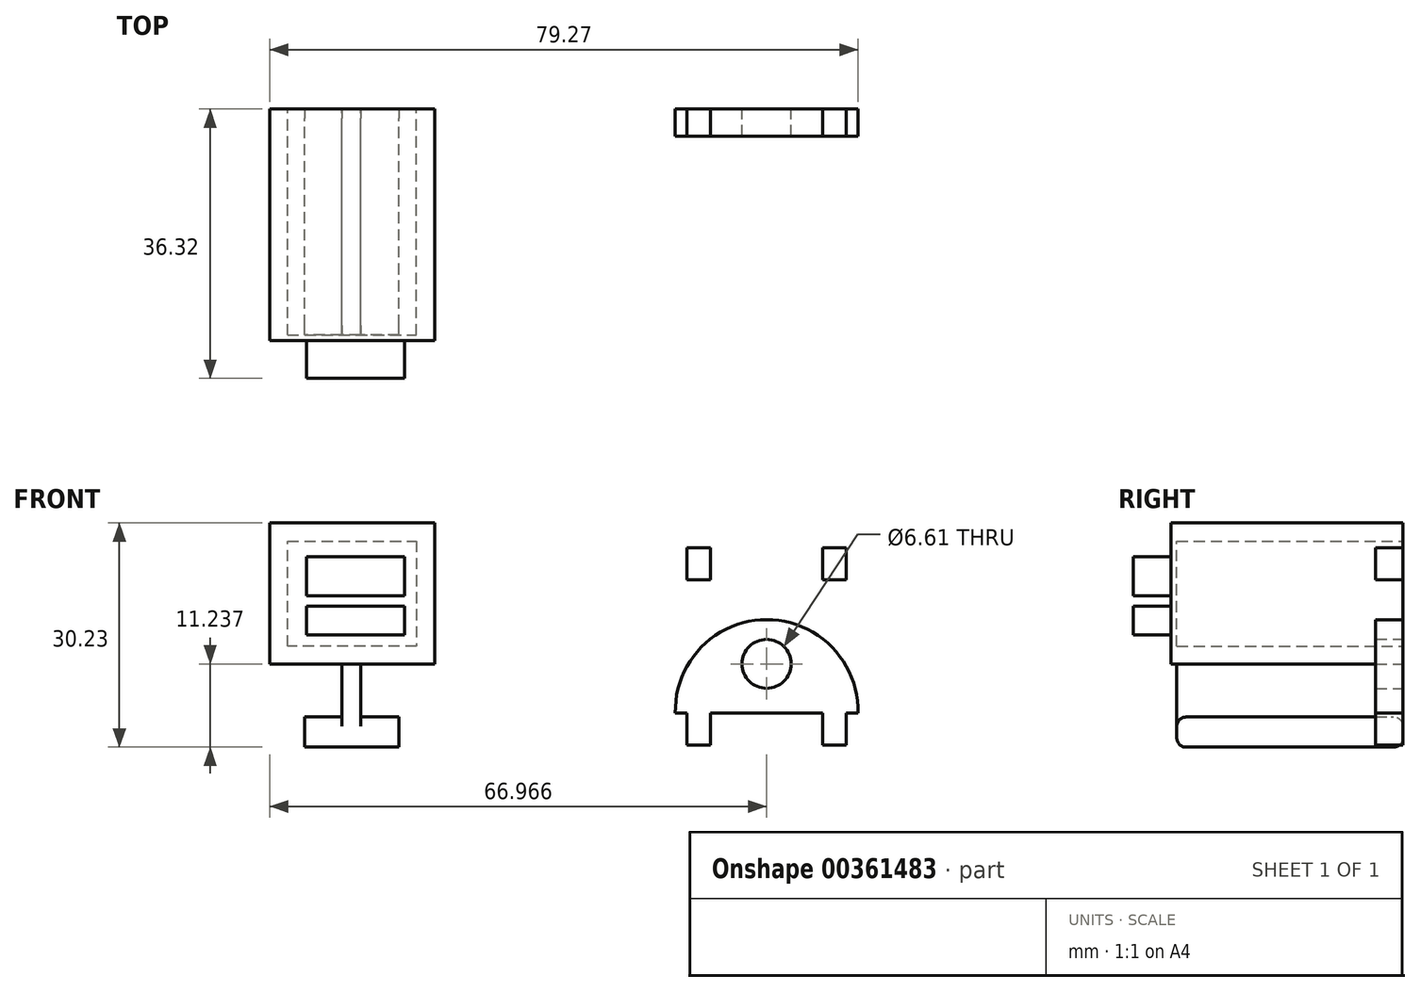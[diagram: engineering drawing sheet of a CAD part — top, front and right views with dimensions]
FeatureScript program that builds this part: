
annotation { "Feature Type Name" : "Feature", "Feature Type Description" : "" }
export const myFeature = defineFeature(function(context is Context, id is Id, definition is map)
    precondition{}
    {
        {
            var Q0;
            Q0=qCreatedBy(makeId("Front.planeOp"),FACE);
            var sketch = newSketch(context, id + "F0", { "sketchPlane" : qUnion([Q0])});
            skLineSegment(sketch, "E0", {"start": v(-32.35, 35.97) * mm, "end": v(-10.13, 35.97) * mm});
            skLineSegment(sketch, "E1", {"start": v(-10.13, 35.97) * mm, "end": v(-10.13, 16.92) * mm});
            skLineSegment(sketch, "E2", {"start": v(-10.13, 16.92) * mm, "end": v(-32.35, 16.92) * mm});
            skLineSegment(sketch, "E3", {"start": v(-32.35, 16.92) * mm, "end": v(-32.35, 35.97) * mm});
            skLineSegment(sketch, "E4", {"start": v(-22.6, 16.92) * mm, "end": v(-22.6, 9.8) * mm});
            skLineSegment(sketch, "E5", {"start": v(-20.06, 16.92) * mm, "end": v(-20.06, 9.8) * mm});
            skLineSegment(sketch, "E6", {"start": v(-22.6, 9.8) * mm, "end": v(-27.6, 9.8) * mm});
            skLineSegment(sketch, "E7", {"start": v(-22.6, 16.92) * mm, "end": v(-20.06, 16.92) * mm});
            skLineSegment(sketch, "E8", {"start": v(-27.6, 9.8) * mm, "end": v(-27.6, 5.74) * mm});
            skLineSegment(sketch, "E9", {"start": v(-27.6, 5.74) * mm, "end": v(-14.9, 5.74) * mm});
            skLineSegment(sketch, "E10", {"start": v(-14.9, 5.74) * mm, "end": v(-14.9, 9.8) * mm});
            skLineSegment(sketch, "E11", {"start": v(-14.9, 9.8) * mm, "end": v(-20.06, 9.8) * mm});
            skLineSegment(sketch, "E12.0", {"start": v(-29.94, 33.55) * mm, "end": v(-12.55, 33.55) * mm});
            skLineSegment(sketch, "E12.1", {"start": v(-29.94, 19.33) * mm, "end": v(-29.94, 33.55) * mm});
            skLineSegment(sketch, "E12.2", {"start": v(-12.55, 19.33) * mm, "end": v(-29.94, 19.33) * mm});
            skLineSegment(sketch, "E12.3", {"start": v(-12.55, 33.55) * mm, "end": v(-12.55, 19.33) * mm});
            skLineSegment(sketch, "E13", {"start": v(-21.33, 16.92) * mm, "end": v(-21.25, 5.74) * mm});
            skSolve(sketch);
        }
        {
            var Q0;
            Q0 = qSketchRegion(id + "F0", true);
            extrude(context, id + "F1", {"entities" : qUnion([Q0]), "depth" : 30.48 * mm});
        }
        {
            var Q0;
            Q0=makeQuery(id+"F1.opExtrude","CAP_FACE",FACE,{"disambiguationData":[OSD([sQuery(id+"F0.wireOp",EDGE,"E0"),sQuery(id+"F0.wireOp",EDGE,"E1"),sQuery(id+"F0.wireOp",EDGE,"E2"),sQuery(id+"F0.wireOp",EDGE,"E3"),sQuery(id+"F0.wireOp",EDGE,"E4"),sQuery(id+"F0.wireOp",EDGE,"E5"),sQuery(id+"F0.wireOp",EDGE,"E6"),sQuery(id+"F0.wireOp",EDGE,"E8"),sQuery(id+"F0.wireOp",EDGE,"E9"),sQuery(id+"F0.wireOp",EDGE,"E10"),sQuery(id+"F0.wireOp",EDGE,"E11"),sQuery(id+"F0.wireOp",EDGE,"E12.0"),sQuery(id+"F0.wireOp",EDGE,"E12.1"),sQuery(id+"F0.wireOp",EDGE,"E12.2"),sQuery(id+"F0.wireOp",EDGE,"E12.3")])],"isStart":false});
            var sketch = newSketch(context, id + "F2", { "sketchPlane" : qUnion([Q0])});
            skLineSegment(sketch, "E14", {"start": v(-32.35, 16.92) * mm, "end": v(-10.13, 16.92) * mm});
            skLineSegment(sketch, "E15", {"start": v(-10.13, 16.92) * mm, "end": v(-10.13, 35.97) * mm});
            skLineSegment(sketch, "E16", {"start": v(-10.13, 35.97) * mm, "end": v(-32.35, 35.97) * mm});
            skLineSegment(sketch, "E17", {"start": v(-32.35, 35.97) * mm, "end": v(-32.35, 16.92) * mm});
            skSolve(sketch);
        }
        {
            var Q0;
            Q0=makeQuery(id+"F2.imprint","IMPRINT",FACE,{"disambiguationData":[TD([[makeQuery(id+"F2.imprint","IMPRINT",EDGE,{"derivedFrom":makeQuery(id+"F1.opExtrude","CAP_EDGE",EDGE,{"disambiguationData":[OSD([sQuery(id+"F0.wireOp",EDGE,"E12.0")])],"isStart":false})}),-1.0]])]});
            var Q1;
            {var subQ0=sQuery(id+"F2.wireOp",EDGE,"E15");Q1=makeQuery(id+"F2.imprint","IMPRINT",FACE,{"disambiguationData":[TD([[makeQuery(id+"F2.imprint","IMPRINT",EDGE,{"derivedFrom":subQ0}),-1.0]])]});}
            extrude(context, id + "F3", {"entities" : qUnion([Q0, Q1]), "operationType" : NewBodyOperationType.ADD, "depth" : 0.76 * mm});
        }
        {
            var Q0;
            Q0=qCreatedBy(makeId("Front.planeOp"),FACE);
            var sketch = newSketch(context, id + "F4", { "sketchPlane" : qUnion([Q0])});
            skLineSegment(sketch, "E18", {"start": v(46.92, 10.37) * mm, "end": v(22.31, 10.37) * mm});
            skArc(sketch, "E19", {"start": v(46.92, 10.37) * mm, "mid": v(34.62, 22.93) * mm, "end": v(22.31, 10.37) * mm});
            skLineSegment(sketch, "E20", {"start": v(46.92, 10.37) * mm, "end": v(45.33, 10.37) * mm});
            skLineSegment(sketch, "E21", {"start": v(22.31, 10.37) * mm, "end": v(23.9, 10.37) * mm});
            skLineSegment(sketch, "E22", {"start": v(45.33, 10.37) * mm, "end": v(45.33, 6.05) * mm});
            skLineSegment(sketch, "E23", {"start": v(45.33, 6.05) * mm, "end": v(42.16, 6.05) * mm});
            skLineSegment(sketch, "E24", {"start": v(42.16, 6.05) * mm, "end": v(42.16, 10.37) * mm});
            skLineSegment(sketch, "E25", {"start": v(23.9, 10.37) * mm, "end": v(23.9, 6.05) * mm});
            skLineSegment(sketch, "E26", {"start": v(23.9, 6.05) * mm, "end": v(27.08, 6.05) * mm});
            skLineSegment(sketch, "E27", {"start": v(27.08, 6.05) * mm, "end": v(27.08, 10.37) * mm});
            skLineSegment(sketch, "E28", {"start": v(34.62, 10.63) * mm, "end": v(34.62, 13.8) * mm});
            skLineSegment(sketch, "E29", {"start": v(34.62, 10.63) * mm, "end": v(34.62, 16.98) * mm});
            skPoint(sketch, "E29.endSnap0", {"position": v(34.62, 12.21) * mm});
            skCircle(sketch, "E30", {"center": v(34.62, 16.98) * mm, "radius": 3.3 * mm});
            skLineSegment(sketch, "E31", {"start": v(46.92, 32.6) * mm, "end": v(22.31, 32.6) * mm});
            skLineSegment(sketch, "E32", {"start": v(22.31, 32.6) * mm, "end": v(23.9, 32.6) * mm});
            skLineSegment(sketch, "E33", {"start": v(45.33, 32.6) * mm, "end": v(46.92, 32.6) * mm});
            skLineSegment(sketch, "E34", {"start": v(23.9, 32.6) * mm, "end": v(23.9, 28.29) * mm});
            skLineSegment(sketch, "E35", {"start": v(23.9, 28.29) * mm, "end": v(27.08, 28.29) * mm});
            skLineSegment(sketch, "E36", {"start": v(27.08, 28.29) * mm, "end": v(27.08, 32.6) * mm});
            skLineSegment(sketch, "E37", {"start": v(42.16, 32.6) * mm, "end": v(42.16, 28.29) * mm});
            skLineSegment(sketch, "E38", {"start": v(42.16, 28.29) * mm, "end": v(45.33, 28.29) * mm});
            skLineSegment(sketch, "E39", {"start": v(45.33, 28.29) * mm, "end": v(45.33, 32.6) * mm});
            skArc(sketch, "E40", {"start": v(46.92, 32.6) * mm, "mid": v(34.62, 44.77) * mm, "end": v(22.31, 32.6) * mm});
            skLineSegment(sketch, "E41", {"start": v(34.62, 32.47) * mm, "end": v(34.62, 35.64) * mm});
            skLineSegment(sketch, "E42", {"start": v(34.62, 32.47) * mm, "end": v(34.62, 38.82) * mm});
            skCircle(sketch, "E43", {"center": v(34.62, 38.82) * mm, "radius": 3.18 * mm});
            skSolve(sketch);
        }
        {
            var Q0;
            Q0=makeQuery(id+"F4.imprint","IMPRINT",FACE,{"disambiguationData":[TD([[makeQuery(id+"F4.imprint","IMPRINT",EDGE,{"derivedFrom":sQuery(id+"F4.wireOp",EDGE,"E19")}),1.0]])]});
            var Q1;
            {var subQ0=sQuery(id+"F4.wireOp",EDGE,"E22");Q1=makeQuery(id+"F4.imprint","IMPRINT",FACE,{"disambiguationData":[TD([[makeQuery(id+"F4.imprint","IMPRINT",EDGE,{"derivedFrom":subQ0}),-1.0]])]});}
            var Q2;
            {var subQ0=sQuery(id+"F4.wireOp",EDGE,"E25");Q2=makeQuery(id+"F4.imprint","IMPRINT",FACE,{"disambiguationData":[TD([[makeQuery(id+"F4.imprint","IMPRINT",EDGE,{"derivedFrom":subQ0}),1.0]])]});}
            var Q3;
            {var subQ0=sQuery(id+"F4.wireOp",EDGE,"E32");Q3=makeQuery(id+"F4.imprint","IMPRINT",FACE,{"disambiguationData":[TD([[makeQuery(id+"F4.imprint","IMPRINT",EDGE,{"derivedFrom":subQ0}),1.0]])]});}
            var Q4;
            {var subQ2=sQuery(id+"F4.wireOp",EDGE,"E37");Q4=makeQuery(id+"F4.imprint","IMPRINT",FACE,{"disambiguationData":[TD([[makeQuery(id+"F4.imprint","IMPRINT",EDGE,{"derivedFrom":subQ2}),1.0]])]});}
            var Q5;
            {var subQ0=sQuery(id+"F4.wireOp",EDGE,"E34");Q5=makeQuery(id+"F4.imprint","IMPRINT",FACE,{"disambiguationData":[TD([[makeQuery(id+"F4.imprint","IMPRINT",EDGE,{"derivedFrom":subQ0}),1.0]])]});}
            extrude(context, id + "F5", {"entities" : qUnion([Q0, Q1, Q2, Q3, Q4, Q5]), "operationType" : NewBodyOperationType.ADD, "depth" : 3.66 * mm});
        }
        {
            var Q0;
            Q0=makeQuery(id+"F1.opExtrude","CAP_EDGE",EDGE,{"disambiguationData":[OSD([sQuery(id+"F0.wireOp",EDGE,"E11")])],"isStart":true});
            var Q1;
            Q1=makeQuery(id+"F1.opExtrude","CAP_EDGE",EDGE,{"disambiguationData":[OSD([sQuery(id+"F0.wireOp",EDGE,"E6")])],"isStart":false});
            var Q2;
            Q2=makeQuery(id+"F1.opExtrude","CAP_EDGE",EDGE,{"disambiguationData":[OSD([sQuery(id+"F0.wireOp",EDGE,"E9")])],"isStart":false});
            var Q3;
            Q3=makeQuery(id+"F1.opExtrude","CAP_EDGE",EDGE,{"disambiguationData":[OSD([sQuery(id+"F0.wireOp",EDGE,"E9")])],"isStart":true});
            var Q4;
            Q4=makeQuery(id+"F1.opExtrude","CAP_EDGE",EDGE,{"disambiguationData":[OSD([sQuery(id+"F0.wireOp",EDGE,"E11")])],"isStart":false});
            var Q5;
            Q5=makeQuery(id+"F1.opExtrude","CAP_EDGE",EDGE,{"disambiguationData":[OSD([sQuery(id+"F0.wireOp",EDGE,"E6")])],"isStart":true});
            fillet(context, id + "F6", {"entities" : qUnion([Q0, Q1, Q2, Q3, Q4, Q5]), "radius" : 1.27 * mm, "tangentPropagation" : true, "allowEdgeOverflow" : false});
        }
        {
            var Q0;
            Q0=makeQuery(id+"F3.opExtrude","CAP_FACE",FACE,{"disambiguationData":[OSD([sQuery(id+"F2.wireOp",EDGE,"E14"),sQuery(id+"F2.wireOp",EDGE,"E15"),sQuery(id+"F2.wireOp",EDGE,"E16"),sQuery(id+"F2.wireOp",EDGE,"E17")])],"isStart":false});
            var sketch = newSketch(context, id + "F7", { "sketchPlane" : qUnion([Q0])});
            skLineSegment(sketch, "E44.bottom", {"start": v(-27.39, 31.42) * mm, "end": v(-14.14, 31.42) * mm});
            skLineSegment(sketch, "E44.top", {"start": v(-27.39, 26.17) * mm, "end": v(-14.14, 26.17) * mm});
            skLineSegment(sketch, "E44.left", {"start": v(-27.39, 31.42) * mm, "end": v(-27.39, 26.17) * mm});
            skLineSegment(sketch, "E44.right", {"start": v(-14.14, 31.42) * mm, "end": v(-14.14, 26.17) * mm});
            skLineSegment(sketch, "E45.bottom", {"start": v(-27.39, 24.76) * mm, "end": v(-14.14, 24.76) * mm});
            skLineSegment(sketch, "E45.top", {"start": v(-27.39, 20.86) * mm, "end": v(-14.14, 20.86) * mm});
            skLineSegment(sketch, "E45.left", {"start": v(-27.39, 24.76) * mm, "end": v(-27.39, 20.86) * mm});
            skLineSegment(sketch, "E45.right", {"start": v(-14.14, 24.76) * mm, "end": v(-14.14, 20.86) * mm});
            skSolve(sketch);
        }
        {
            var Q0;
            Q0 = qSketchRegion(id + "F7", true);
            extrude(context, id + "F8", {"entities" : qUnion([Q0]), "operationType" : NewBodyOperationType.ADD, "depth" : 5.08 * mm});
        }
    });
